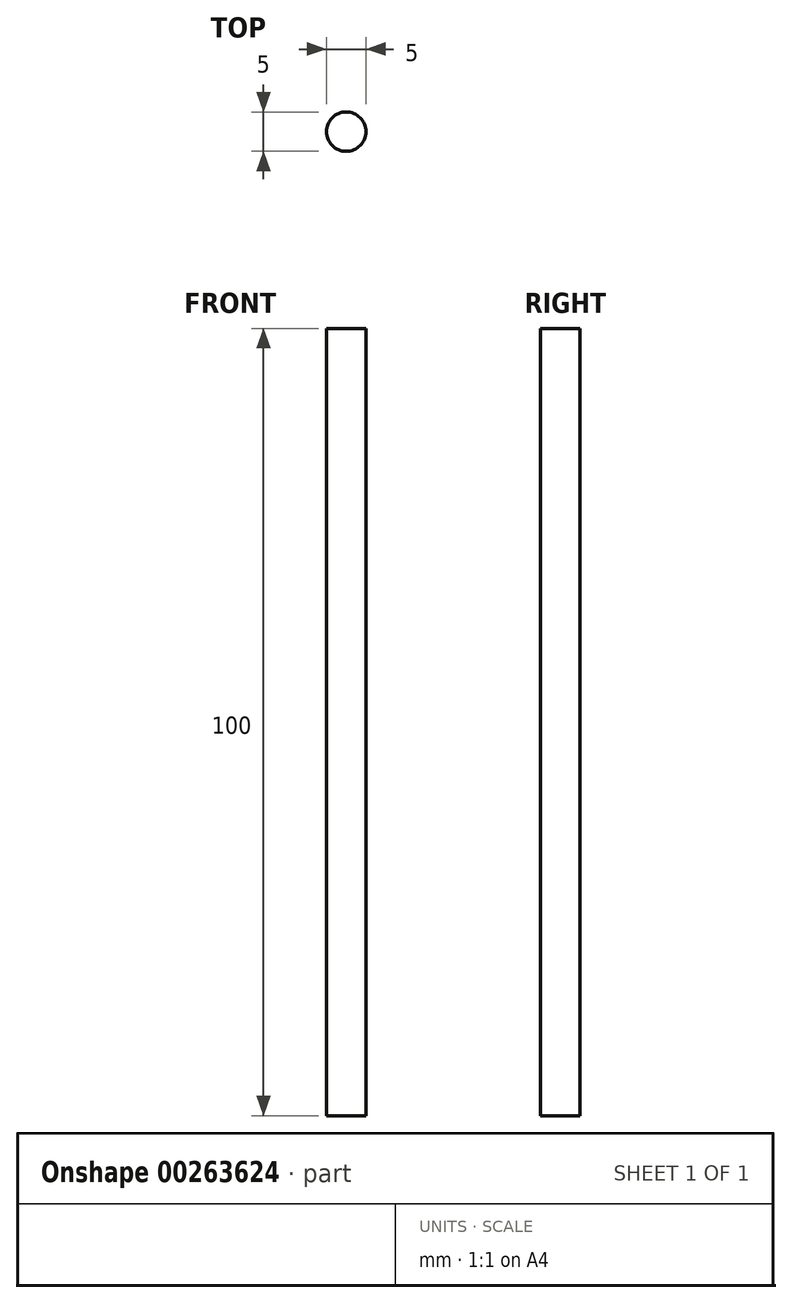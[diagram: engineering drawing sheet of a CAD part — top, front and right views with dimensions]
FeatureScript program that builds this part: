
annotation { "Feature Type Name" : "Feature", "Feature Type Description" : "" }
export const myFeature = defineFeature(function(context is Context, id is Id, definition is map)
    precondition{}
    {
        {
            var Q0;
            Q0=qCreatedBy(makeId("Top.planeOp"),FACE);
            var sketch = newSketch(context, id + "F0", { "sketchPlane" : qUnion([Q0])});
            skCircle(sketch, "E0", {"center": v(0, 0) * mm, "radius": 2.5 * mm});
            skSolve(sketch);
        }
        {
            var Q0;
            Q0 = qSketchRegion(id + "F0", true);
            extrude(context, id + "F1", {"entities" : qUnion([Q0]), "oppositeDirection" : true, "depth" : 100 * mm});
        }
    });
